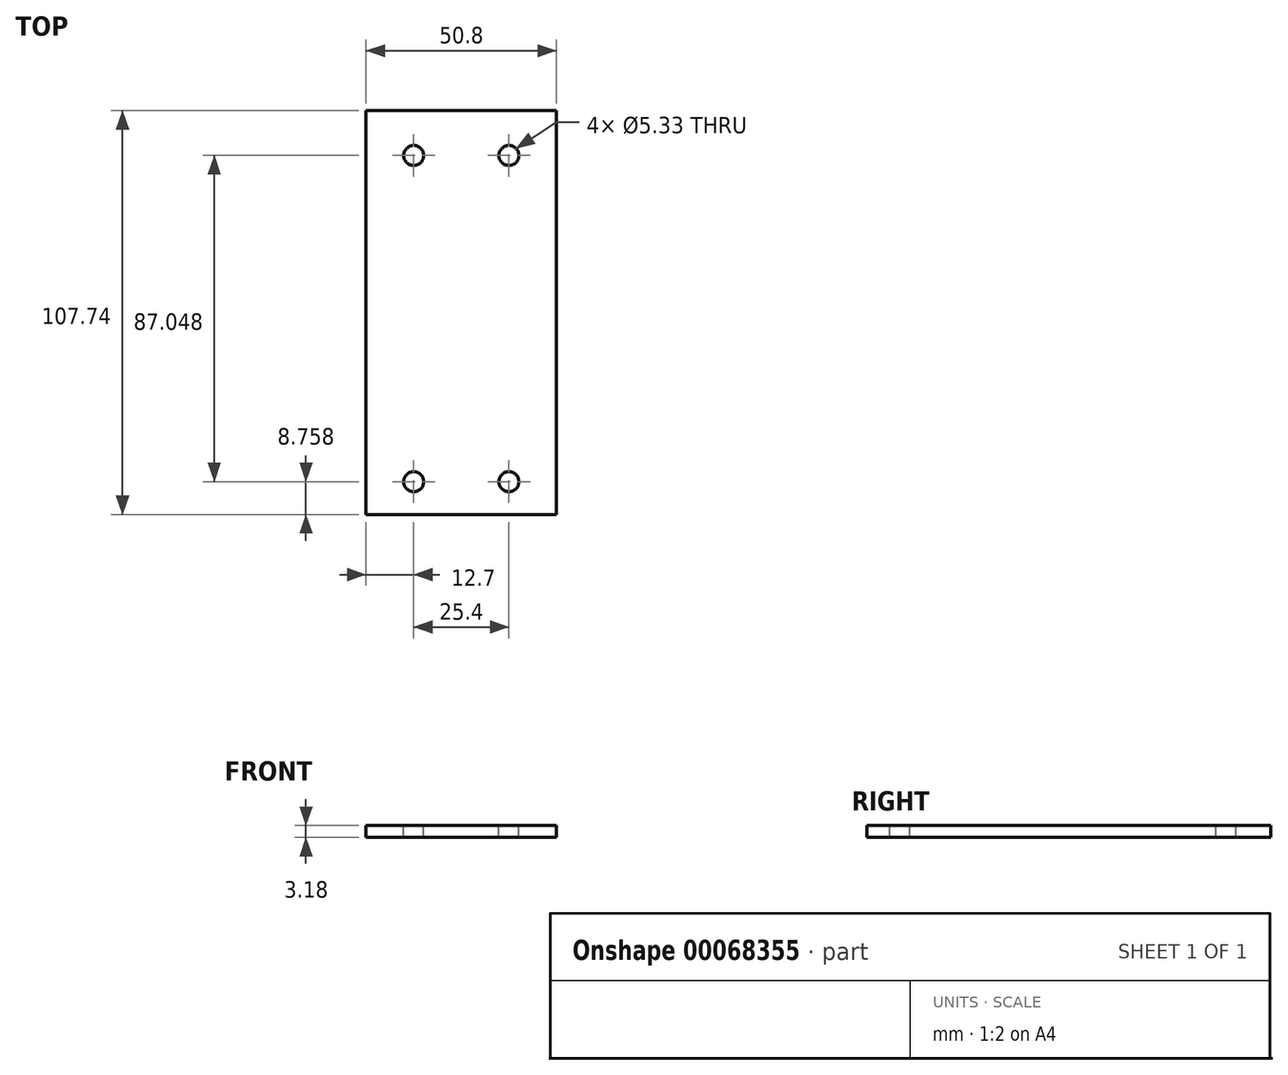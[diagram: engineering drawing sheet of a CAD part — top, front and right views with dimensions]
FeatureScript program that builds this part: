
annotation { "Feature Type Name" : "Feature", "Feature Type Description" : "" }
export const myFeature = defineFeature(function(context is Context, id is Id, definition is map)
    precondition{}
    {
        {
            var Q0;
            Q0=qCreatedBy(makeId("Top.planeOp"),FACE);
            var sketch = newSketch(context, id + "F0", { "sketchPlane" : qUnion([Q0])});
            skLineSegment(sketch, "E0.bottom", {"start": v(25.4, -53.87) * mm, "end": v(-25.4, -53.87) * mm});
            skLineSegment(sketch, "E0.top", {"start": v(25.4, 53.87) * mm, "end": v(-25.4, 53.87) * mm});
            skLineSegment(sketch, "E0.left", {"start": v(25.4, -53.87) * mm, "end": v(25.4, 53.87) * mm});
            skLineSegment(sketch, "E0.right", {"start": v(-25.4, -53.87) * mm, "end": v(-25.4, 53.87) * mm});
            skPoint(sketch, "E0.middle", {"position": v(0, 0) * mm});
            skSolve(sketch);
        }
        {
            var Q0;
            Q0 = qSketchRegion(id + "F0", true);
            extrude(context, id + "F1", {"entities" : qUnion([Q0]), "depth" : 3.17 * mm});
        }
        {
            var Q0;
            Q0=makeQuery(id+"F1.opExtrude","CAP_FACE",FACE,{"disambiguationData":[OSD([sQuery(id+"F0.wireOp",EDGE,"E0.bottom"),sQuery(id+"F0.wireOp",EDGE,"E0.top"),sQuery(id+"F0.wireOp",EDGE,"E0.left"),sQuery(id+"F0.wireOp",EDGE,"E0.right")])],"isStart":false});
            var sketch = newSketch(context, id + "F2", { "sketchPlane" : qUnion([Q0])});
            skCircle(sketch, "E1", {"center": v(12.7, -45.11) * mm, "radius": 2.67 * mm});
            skCircle(sketch, "E2", {"center": v(-12.7, -45.11) * mm, "radius": 2.67 * mm});
            skCircle(sketch, "E3", {"center": v(12.7, 41.94) * mm, "radius": 2.67 * mm});
            skCircle(sketch, "E4", {"center": v(-12.7, 41.94) * mm, "radius": 2.67 * mm});
            skSolve(sketch);
        }
        {
            var Q0;
            Q0 = qSketchRegion(id + "F2", true);
            var Q1;
            Q1=sQuery(id+"F2.wireOp",EDGE,"E4");
            var Q2;
            Q2=sQuery(id+"F2.wireOp",EDGE,"E3");
            var Q3;
            Q3=sQuery(id+"F2.wireOp",EDGE,"E1");
            var Q4;
            Q4=sQuery(id+"F2.wireOp",EDGE,"E2");
            extrude(context, id + "F3", {"entities" : qUnion([Q0]), "operationType" : NewBodyOperationType.REMOVE, "surfaceEntities" : qUnion([Q1, Q2, Q3, Q4]), "oppositeDirection" : true, "depth" : 3.17 * mm});
        }
    });
